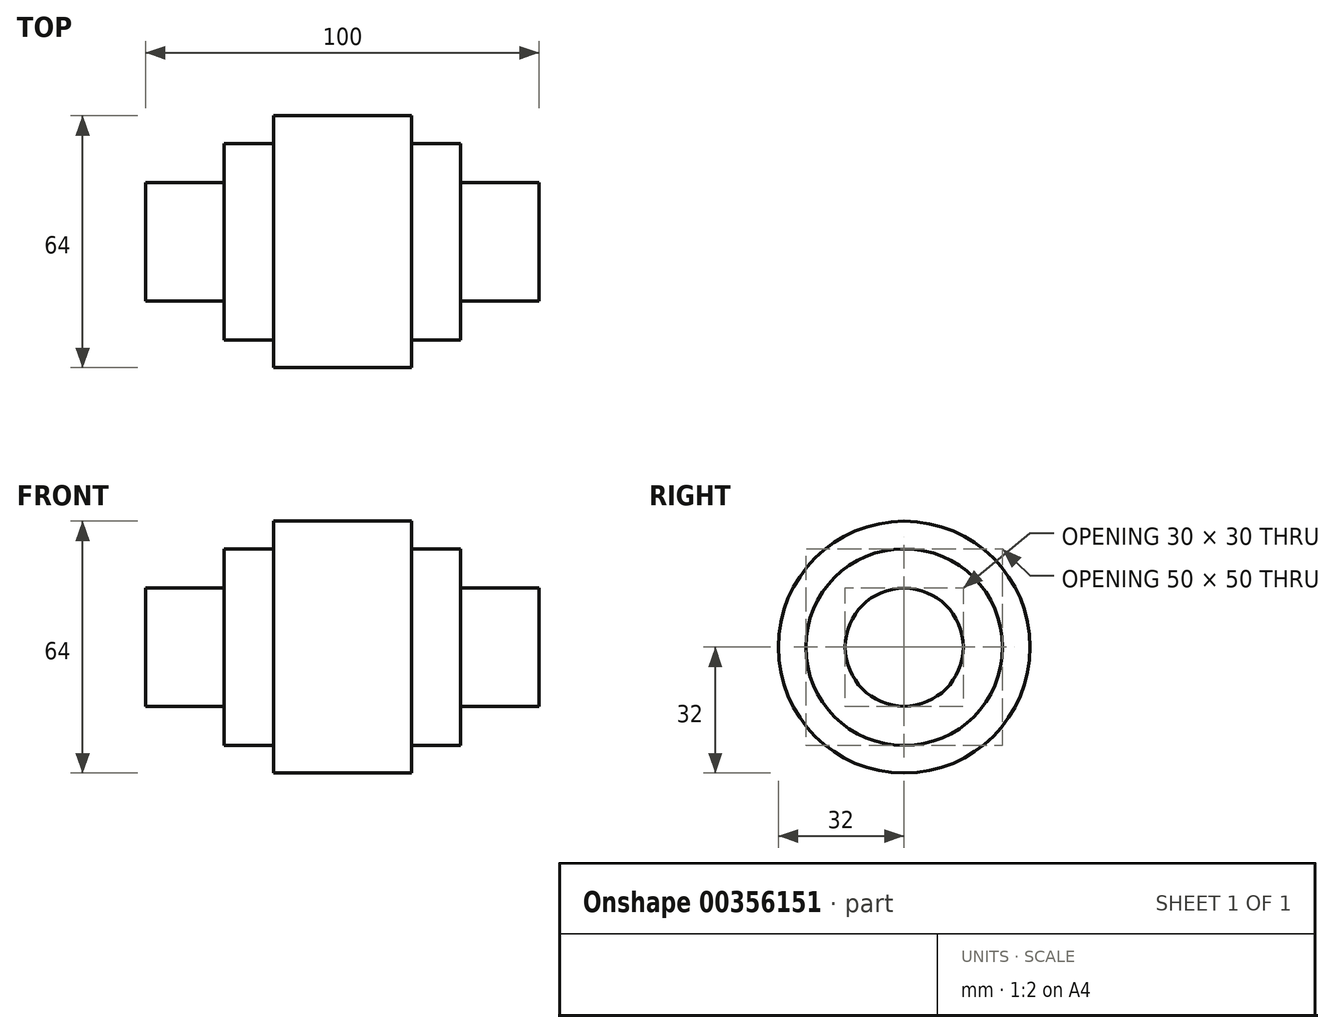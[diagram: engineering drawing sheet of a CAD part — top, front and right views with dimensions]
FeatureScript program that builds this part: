
annotation { "Feature Type Name" : "Feature", "Feature Type Description" : "" }
export const myFeature = defineFeature(function(context is Context, id is Id, definition is map)
    precondition{}
    {
        {
            var Q0;
            Q0=qCreatedBy(makeId("Front.planeOp"),FACE);
            var sketch = newSketch(context, id + "F0", { "sketchPlane" : qUnion([Q0])});
            skLineSegment(sketch, "E0.bottom", {"start": v(-50, 15) * mm, "end": v(50, 15) * mm});
            skLineSegment(sketch, "E0.top", {"start": v(-50, 0) * mm, "end": v(50, 0) * mm});
            skLineSegment(sketch, "E0.left", {"start": v(-50, 15) * mm, "end": v(-50, 0) * mm});
            skLineSegment(sketch, "E0.right", {"start": v(50, 15) * mm, "end": v(50, 0) * mm});
            skLineSegment(sketch, "E1", {"start": v(50, 0) * mm, "end": v(-50, 0) * mm});
            skPoint(sketch, "E2.orphan", {"position": v(86.18, 0) * mm});
            skPoint(sketch, "E3.orphan", {"position": v(-86.67, 0) * mm});
            skLineSegment(sketch, "E4", {"start": v(-86.67, 0) * mm, "end": v(86.18, 0) * mm, "construction": true});
            skSolve(sketch);
        }
        {
            var Q0;
            Q0=makeQuery(id+"F0.imprint","IMPRINT",FACE,{"disambiguationData":[TD([[makeQuery(id+"F0.imprint","IMPRINT",EDGE,{"derivedFrom":sQuery(id+"F0.wireOp",EDGE,"E0.bottom")}),-1.0]])]});
            var Q1;
            Q1=sQuery(id+"F0.wireOp",EDGE,"E4");
            revolve(context, id + "F1", {"entities" : qUnion([Q0]), "axis" : qUnion([Q1]), "revolveType" : RevolveType.FULL});
        }
        {
            var Q0;
            Q0=qCreatedBy(makeId("Front.planeOp"),FACE);
            var sketch = newSketch(context, id + "F2", { "sketchPlane" : qUnion([Q0])});
            skLineSegment(sketch, "E5", {"start": v(116.59, 0) * mm, "end": v(-83.04, 0) * mm, "construction": true});
            skLineSegment(sketch, "E6.bottom", {"start": v(-30, 0) * mm, "end": v(30, 0) * mm});
            skLineSegment(sketch, "E6.top", {"start": v(-30, 25) * mm, "end": v(30, 25) * mm});
            skLineSegment(sketch, "E6.left", {"start": v(-30, 0) * mm, "end": v(-30, 25) * mm});
            skLineSegment(sketch, "E6.right", {"start": v(30, 0) * mm, "end": v(30, 25) * mm});
            skSolve(sketch);
        }
        {
            var Q0;
            Q0 = qSketchRegion(id + "F2", true);
            var Q1;
            Q1=sQuery(id+"F2.wireOp",EDGE,"E5");
            revolve(context, id + "F3", {"operationType" : NewBodyOperationType.ADD, "entities" : qUnion([Q0]), "axis" : qUnion([Q1]), "revolveType" : RevolveType.FULL});
        }
        {
            var Q0;
            Q0=qCreatedBy(makeId("Front.planeOp"),FACE);
            var sketch = newSketch(context, id + "F4", { "sketchPlane" : qUnion([Q0])});
            skLineSegment(sketch, "E7.bottom", {"start": v(-17.5, 0) * mm, "end": v(17.5, 0) * mm});
            skLineSegment(sketch, "E7.top", {"start": v(-17.5, 32) * mm, "end": v(17.5, 32) * mm});
            skLineSegment(sketch, "E7.left", {"start": v(-17.5, 0) * mm, "end": v(-17.5, 32) * mm});
            skLineSegment(sketch, "E7.right", {"start": v(17.5, 0) * mm, "end": v(17.5, 32) * mm});
            skLineSegment(sketch, "E8", {"start": v(-73.3, 0) * mm, "end": v(89.8, 0) * mm, "construction": true});
            skSolve(sketch);
        }
        {
            var Q0;
            Q0=makeQuery(id+"F4.imprint","IMPRINT",FACE,{"disambiguationData":[TD([[makeQuery(id+"F4.imprint","IMPRINT",EDGE,{"derivedFrom":sQuery(id+"F4.wireOp",EDGE,"E7.bottom")}),1.0]])]});
            var Q1;
            Q1=sQuery(id+"F4.wireOp",EDGE,"E8");
            revolve(context, id + "F5", {"operationType" : NewBodyOperationType.ADD, "entities" : qUnion([Q0]), "axis" : qUnion([Q1]), "revolveType" : RevolveType.FULL});
        }
    });
